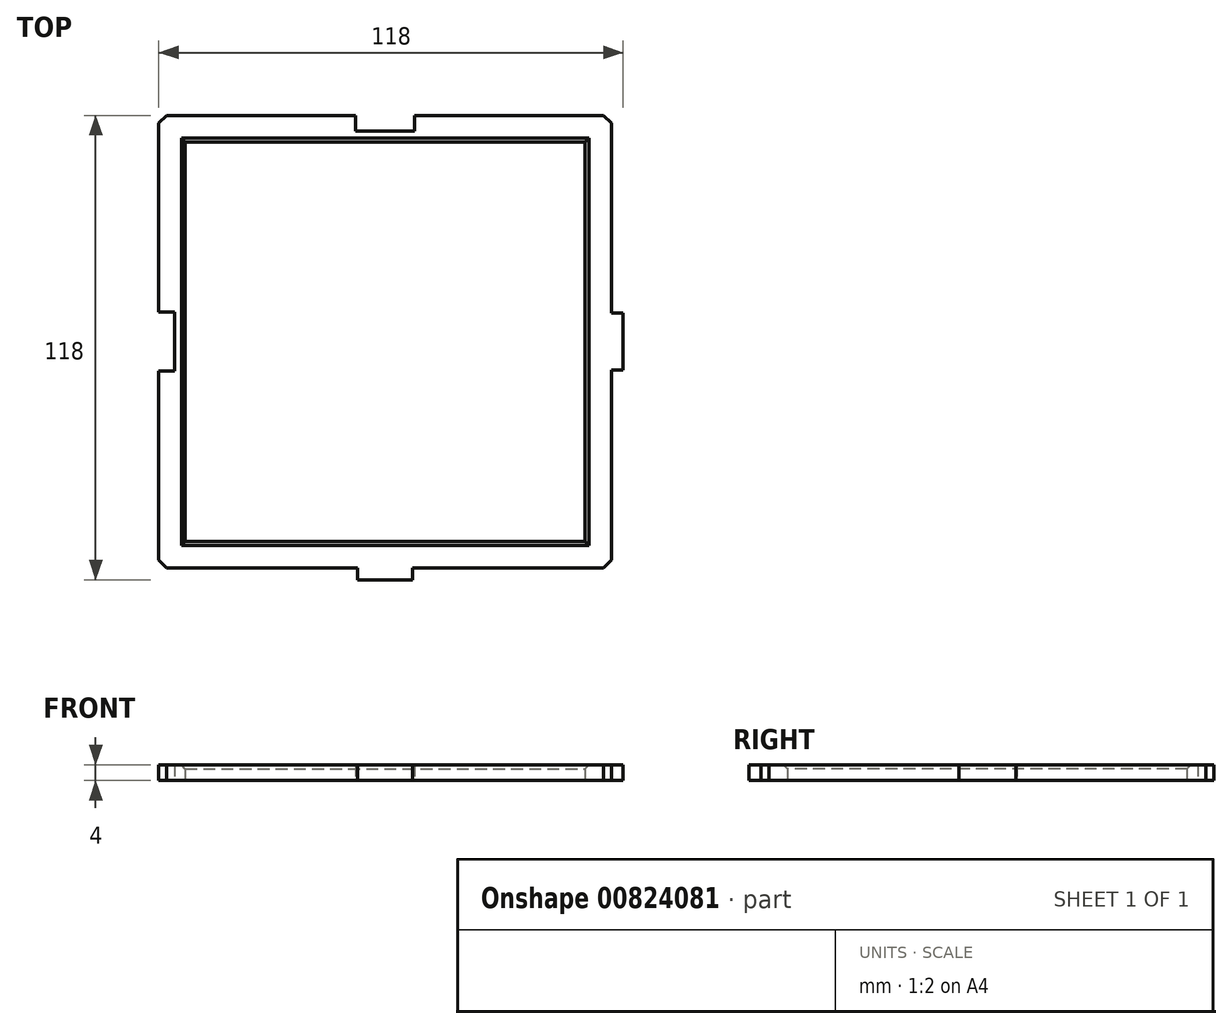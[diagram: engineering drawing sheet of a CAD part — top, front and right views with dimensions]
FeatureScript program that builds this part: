
annotation { "Feature Type Name" : "Feature", "Feature Type Description" : "" }
export const myFeature = defineFeature(function(context is Context, id is Id, definition is map)
    precondition{}
    {
        {
            var Q0;
            Q0=qCreatedBy(makeId("Top.planeOp"),FACE);
            var sketch = newSketch(context, id + "F0", { "sketchPlane" : qUnion([Q0])});
            skLineSegment(sketch, "E0.top", {"start": v(-50.75, -50.75) * mm, "end": v(50.75, -50.75) * mm});
            skLineSegment(sketch, "E0.left", {"start": v(-50.75, 50.75) * mm, "end": v(-50.75, -50.75) * mm});
            skLineSegment(sketch, "E0.right", {"start": v(50.75, 50.75) * mm, "end": v(50.75, -50.75) * mm});
            skLineSegment(sketch, "E1.bottom", {"start": v(-57.5, 57.5) * mm, "end": v(-7.5, 57.5) * mm});
            skLineSegment(sketch, "E1.top", {"start": v(-57.5, -57.5) * mm, "end": v(-7, -57.5) * mm});
            skLineSegment(sketch, "E1.left", {"start": v(-57.5, 57.5) * mm, "end": v(-57.5, 7.5) * mm});
            skLineSegment(sketch, "E1.right", {"start": v(57.5, 57.5) * mm, "end": v(57.5, 7.25) * mm});
            skLineSegment(sketch, "E2", {"start": v(-57.5, 7.5) * mm, "end": v(-53.5, 7.5) * mm});
            skLineSegment(sketch, "E3", {"start": v(-53.5, 7.5) * mm, "end": v(-53.5, -7.5) * mm});
            skLineSegment(sketch, "E4", {"start": v(-53.5, -7.5) * mm, "end": v(-57.5, -7.5) * mm});
            skLineSegment(sketch, "E5", {"start": v(57.5, 7.25) * mm, "end": v(60.5, 7.25) * mm});
            skLineSegment(sketch, "E6", {"start": v(60.5, 7.25) * mm, "end": v(60.5, -7.25) * mm});
            skLineSegment(sketch, "E7", {"start": v(60.5, -7.25) * mm, "end": v(57.5, -7.25) * mm});
            skLineSegment(sketch, "E8", {"start": v(-7, -57.5) * mm, "end": v(-7, -60.5) * mm});
            skLineSegment(sketch, "E9", {"start": v(-7, -60.5) * mm, "end": v(7, -60.5) * mm});
            skLineSegment(sketch, "E10", {"start": v(7, -60.5) * mm, "end": v(7, -57.5) * mm});
            skLineSegment(sketch, "E11", {"start": v(-7.5, 57.5) * mm, "end": v(-7.5, 53.5) * mm});
            skLineSegment(sketch, "E12", {"start": v(-7.5, 53.5) * mm, "end": v(7.5, 53.5) * mm});
            skLineSegment(sketch, "E13", {"start": v(7.5, 53.5) * mm, "end": v(7.5, 57.5) * mm});
            skLineSegment(sketch, "E14.trimOffspring", {"start": v(-57.5, -7.5) * mm, "end": v(-57.5, -57.5) * mm});
            skLineSegment(sketch, "E15.trimOffspring", {"start": v(7.5, 57.5) * mm, "end": v(57.5, 57.5) * mm});
            skLineSegment(sketch, "E16.trimOffspring", {"start": v(7, -57.5) * mm, "end": v(57.5, -57.5) * mm});
            skLineSegment(sketch, "E17.trimOffspring", {"start": v(57.5, -7.25) * mm, "end": v(57.5, -57.5) * mm});
            skLineSegment(sketch, "E18", {"start": v(-50.75, 50.75) * mm, "end": v(50.75, 50.75) * mm});
            skSolve(sketch);
        }
        {
            var Q0;
            Q0=makeQuery(id+"F0.imprint","IMPRINT",FACE,{"disambiguationData":[TD([[makeQuery(id+"F0.imprint","IMPRINT",EDGE,{"derivedFrom":sQuery(id+"F0.wireOp",EDGE,"E0.top")}),-1.0]])]});
            extrude(context, id + "F1", {"entities" : qUnion([Q0]), "depth" : 4 * mm, "offsetDistance" : 25 * mm});
        }
        {
            var Q0;
            Q0=makeQuery(id+"F1.opExtrude","SWEPT_EDGE",EDGE,{"disambiguationData":[OSD([sQuery(id+"F0.wireOp",EDGE,"E1.top"),sQuery(id+"F0.wireOp",EDGE,"E14.trimOffspring")])]});
            var Q1;
            Q1=makeQuery(id+"F1.opExtrude","SWEPT_EDGE",EDGE,{"disambiguationData":[OSD([sQuery(id+"F0.wireOp",EDGE,"E16.trimOffspring"),sQuery(id+"F0.wireOp",EDGE,"E17.trimOffspring")])]});
            var Q2;
            Q2=makeQuery(id+"F1.opExtrude","SWEPT_EDGE",EDGE,{"disambiguationData":[OSD([sQuery(id+"F0.wireOp",EDGE,"E1.right"),sQuery(id+"F0.wireOp",EDGE,"E15.trimOffspring")])]});
            var Q3;
            Q3=makeQuery(id+"F1.opExtrude","SWEPT_EDGE",EDGE,{"disambiguationData":[OSD([sQuery(id+"F0.wireOp",EDGE,"E1.bottom"),sQuery(id+"F0.wireOp",EDGE,"E1.left")])]});
            chamfer(context, id + "F2", {"entities" : qUnion([Q0, Q1, Q2, Q3]), "width" : 2 * mm, "tangentPropagation" : true});
        }
        {
            var Q0;
            Q0=makeQuery(id+"F1.opExtrude","CAP_EDGE",EDGE,{"disambiguationData":[OSD([sQuery(id+"F0.wireOp",EDGE,"E0.left")])],"isStart":false});
            var Q1;
            Q1=makeQuery(id+"F1.opExtrude","CAP_EDGE",EDGE,{"disambiguationData":[OSD([sQuery(id+"F0.wireOp",EDGE,"E18")])],"isStart":false});
            var Q2;
            Q2=makeQuery(id+"F1.opExtrude","CAP_EDGE",EDGE,{"disambiguationData":[OSD([sQuery(id+"F0.wireOp",EDGE,"E0.right")])],"isStart":false});
            var Q3;
            Q3=makeQuery(id+"F1.opExtrude","CAP_EDGE",EDGE,{"disambiguationData":[OSD([sQuery(id+"F0.wireOp",EDGE,"E0.top")])],"isStart":false});
            chamfer(context, id + "F3", {"entities" : qUnion([Q0, Q1, Q2, Q3]), "width" : 1 * mm, "tangentPropagation" : true});
        }
    });
